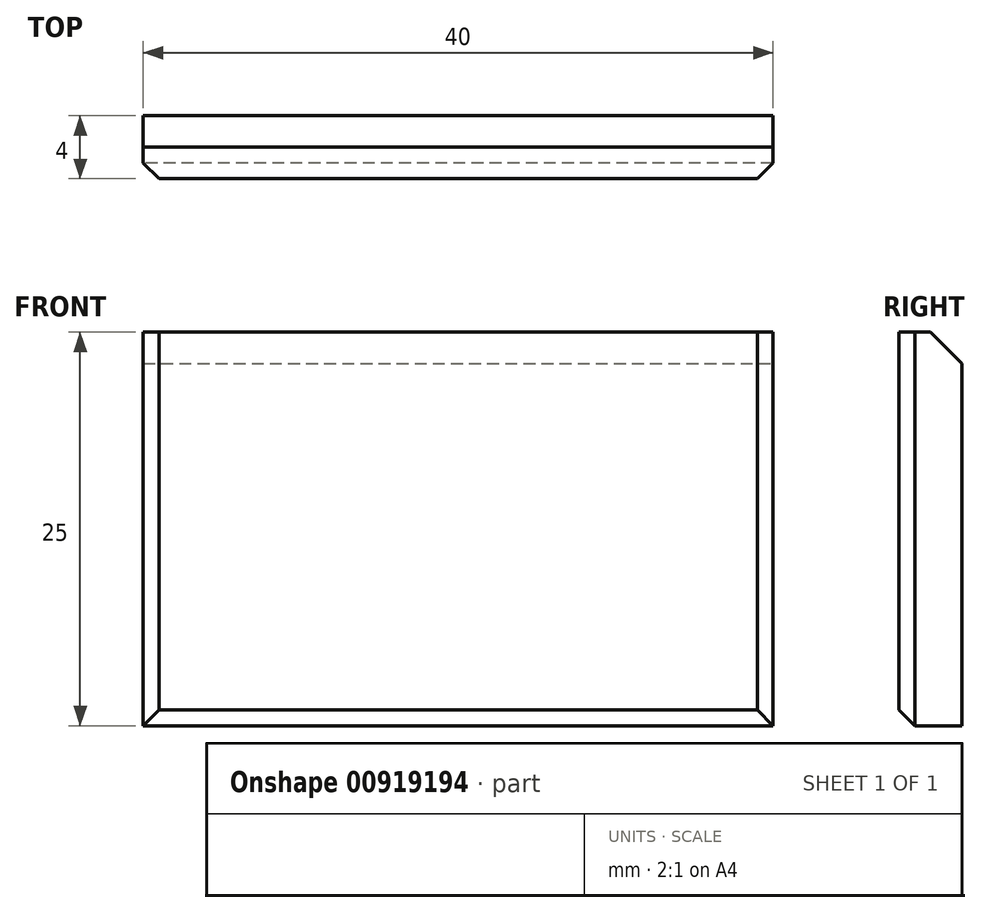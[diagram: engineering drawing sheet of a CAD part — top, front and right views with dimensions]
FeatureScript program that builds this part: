
annotation { "Feature Type Name" : "Feature", "Feature Type Description" : "" }
export const myFeature = defineFeature(function(context is Context, id is Id, definition is map)
    precondition{}
    {
        {
            var Q0;
            Q0=qCreatedBy(makeId("Front.planeOp"),FACE);
            var sketch = newSketch(context, id + "F0", { "sketchPlane" : qUnion([Q0])});
            skLineSegment(sketch, "E0.bottom", {"start": v(0, 0) * mm, "end": v(40, 0) * mm});
            skLineSegment(sketch, "E0.top", {"start": v(0, 25) * mm, "end": v(40, 25) * mm});
            skLineSegment(sketch, "E0.left", {"start": v(0, 0) * mm, "end": v(0, 25) * mm});
            skLineSegment(sketch, "E0.right", {"start": v(40, 0) * mm, "end": v(40, 25) * mm});
            skSolve(sketch);
        }
        {
            var Q0;
            Q0=makeQuery(id+"F0.imprint","IMPRINT",FACE,{"disambiguationData":[TD([[makeQuery(id+"F0.imprint","IMPRINT",EDGE,{"derivedFrom":sQuery(id+"F0.wireOp",EDGE,"E0.bottom")}),1.0]])]});
            extrude(context, id + "F1", {"entities" : qUnion([Q0]), "depth" : 4 * mm, "offsetDistance" : 25 * mm});
        }
        {
            var Q0;
            Q0=makeQuery(id+"F1.opExtrude","CAP_EDGE",EDGE,{"disambiguationData":[OSD([sQuery(id+"F0.wireOp",EDGE,"E0.left")])],"isStart":false});
            var Q1;
            Q1=makeQuery(id+"F1.opExtrude","CAP_EDGE",EDGE,{"disambiguationData":[OSD([sQuery(id+"F0.wireOp",EDGE,"E0.bottom")])],"isStart":false});
            var Q2;
            Q2=makeQuery(id+"F1.opExtrude","CAP_EDGE",EDGE,{"disambiguationData":[OSD([sQuery(id+"F0.wireOp",EDGE,"E0.right")])],"isStart":false});
            chamfer(context, id + "F2", {"entities" : qUnion([Q0, Q1, Q2]), "width" : 1 * mm, "tangentPropagation" : true});
        }
        {
            var Q0;
            Q0=makeQuery(id+"F1.opExtrude","CAP_EDGE",EDGE,{"disambiguationData":[OSD([sQuery(id+"F0.wireOp",EDGE,"E0.top")])],"isStart":true});
            chamfer(context, id + "F3", {"entities" : qUnion([Q0]), "width" : 2 * mm, "tangentPropagation" : true});
        }
    });
